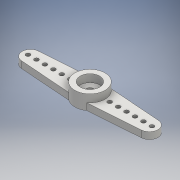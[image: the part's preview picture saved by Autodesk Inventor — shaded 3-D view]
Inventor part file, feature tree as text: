
AUTODESK INVENTOR PART (.ipt)
format: ipt  version: 2016 (Build 200138000, 138)  size: 172,544 bytes
history: native  units: mm
features: extrude x5, sketch x5, other x1
ambient origin geometry x8: Origin, YZ Plane, XZ Plane, XY Plane, X Axis, Y Axis, Z Axis, Center Point
bodies: Body1 (feature_tree)
feature tree (11):
  other  "Sólido1"
  extrude  "Extrusión1"  Depth=1.6mm TaperAngle=0.0deg
  extrude  "Extrusión2"  Depth=0.63mm TaperAngle=0.0deg
  extrude  "Extrusión3"  Depth=1.83mm TaperAngle=0.0deg
  extrude  "Extrusión4"  [1 undecoded]
  extrude  "Extrusión5"  [1 undecoded]
  sketch  "Boceto1"  dims[d8=60.0mm d10=2.0mm d11=10.0mm d13=10.0mm d18=1.6mm d19=0.0mm]
  sketch  "Boceto2"  dims[d21=3.43mm d22=0.0mm d24=0.63mm d25=0.0mm]
  sketch  "Boceto3"  dims[d27=0.63mm d28=0.0mm d30=1.83mm d31=0.0mm]
  sketch  "Boceto4"
  sketch  "Boceto5"
note: 2 required parameter values undecoded (feature->parameter linkage not recoverable at this tier; creation-order binding heuristic only, values carry confidence <= 0.55)
